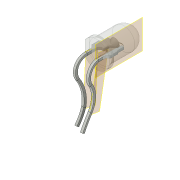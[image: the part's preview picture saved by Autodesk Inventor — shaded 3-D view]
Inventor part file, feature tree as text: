
AUTODESK INVENTOR PART (.ipt)
format: ipt  version: 2016 (Build 200138000, 138)  size: 357,376 bytes
history: native  units: mm
features: sketch x5, plane x3, sweep x3, other x3, projected_geometry x2, extrude x1
ambient origin geometry x8: Origin, YZ Plane, XZ Plane, XY Plane, X Axis, Y Axis, Z Axis, Center Point
bodies: Solid1 (feature_tree), Solid2 (feature_tree)
feature tree (17):
  extrude  "Extrusion1"  TaperAngle=0.0deg  [1 undecoded]
  sketch  "Sketch2"  dims[d6=0.0mm d7=0.0mm]
  plane  "Work Plane1"
  sketch  "Sketch4"
  plane  "Work Plane2"
  sweep  "Sweep3"
  plane  "Work Plane3"
  sweep  "Sweep4"
  sketch  "Sketch1"  dims[d0=26.0mm d1=0.0mm d4=0.0mm d5=0.0mm]
  projected_geometry  "Projected Loop1"
  projected_geometry  "Projected Loop2"
  other  "Work Point1"
  sketch  "Sketch5"
  other  "Work Point2"
  sketch  "Sketch6"
  other  "Cut-Extrude1"
  sweep  "Sweep2"
note: 1 required parameter value undecoded (feature->parameter linkage not recoverable at this tier; creation-order binding heuristic only, values carry confidence <= 0.55)
